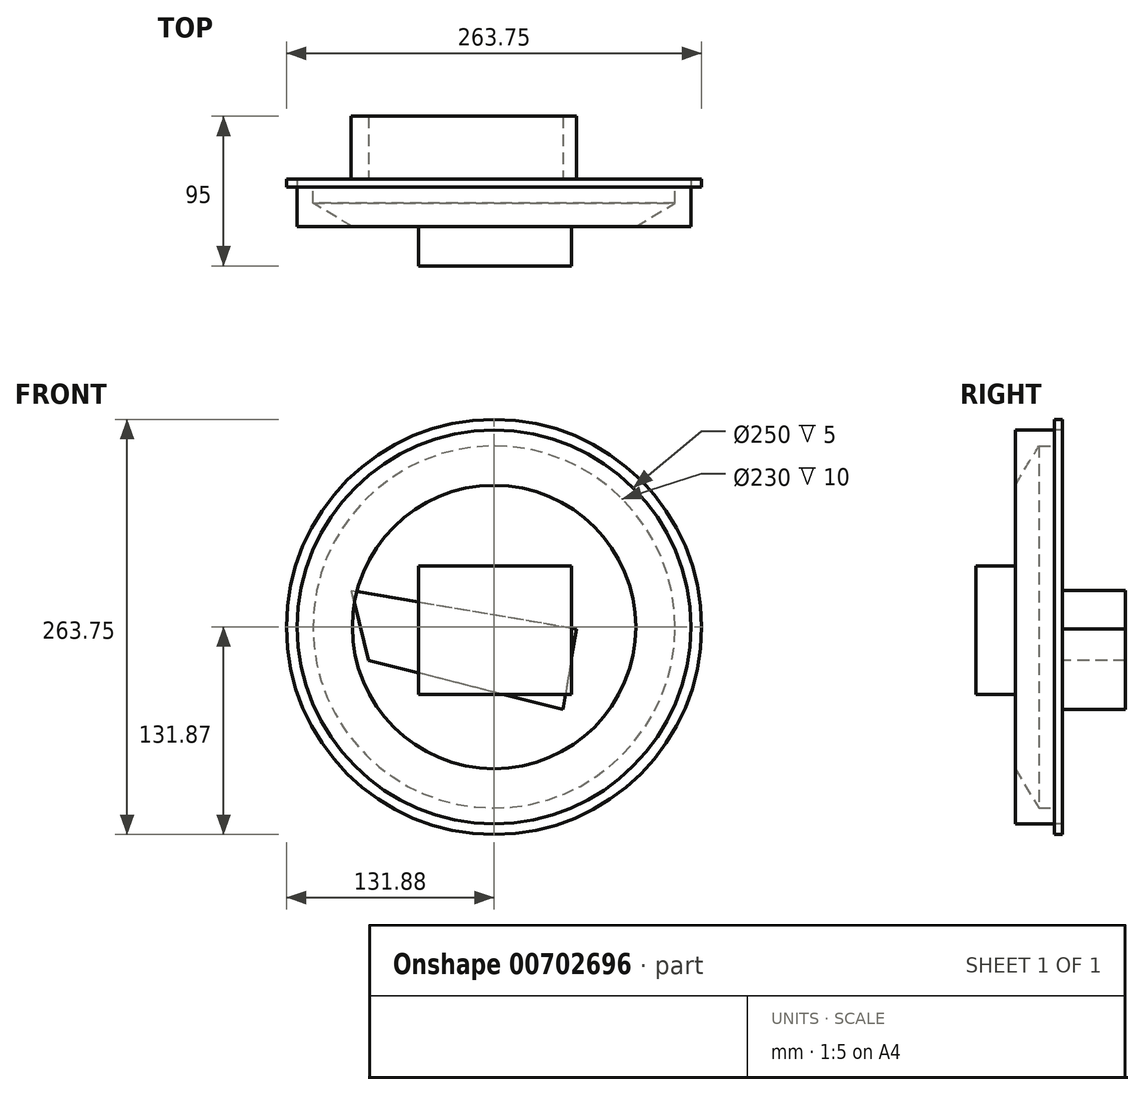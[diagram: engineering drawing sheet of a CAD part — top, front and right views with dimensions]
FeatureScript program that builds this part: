
annotation { "Feature Type Name" : "Feature", "Feature Type Description" : "" }
export const myFeature = defineFeature(function(context is Context, id is Id, definition is map)
    precondition{}
    {
        {
            var Q0;
            Q0=qCreatedBy(makeId("Front.planeOp"),FACE);
            var sketch = newSketch(context, id + "F0", { "sketchPlane" : qUnion([Q0])});
            skCircle(sketch, "E0", {"center": v(-49.3, 42.83) * mm, "radius": 125 * mm});
            skSolve(sketch);
        }
        {
            var Q0;
            Q0=makeQuery(id+"F0.imprint","IMPRINT",FACE,{"disambiguationData":[TD([[makeQuery(id+"F0.imprint","IMPRINT",EDGE,{"derivedFrom":sQuery(id+"F0.wireOp",EDGE,"E0")}),1.0]])]});
            extrude(context, id + "F1", {"entities" : qUnion([Q0]), "depth" : 150 * mm, "offsetDistance" : 25 * mm});
        }
        {
            var Q0;
            Q0=makeQuery(id+"F1.opExtrude","CAP_FACE",FACE,{"disambiguationData":[OSD([sQuery(id+"F0.wireOp",EDGE,"E0")])],"isStart":true});
            var sketch = newSketch(context, id + "F2", { "sketchPlane" : qUnion([Q0])});
            skPoint(sketch, "E1", {"position": v(49.3, 42.83) * mm});
            skCircle(sketch, "E2", {"center": v(49.3, 42.83) * mm, "radius": 131.88 * mm});
            skSolve(sketch);
        }
        {
            var Q0;
            Q0=makeQuery(id+"F2.imprint","IMPRINT",FACE,{"disambiguationData":[TD([[makeQuery(id+"F2.imprint","IMPRINT",EDGE,{"derivedFrom":sQuery(id+"F2.wireOp",EDGE,"E2")}),1.0]])]});
            extrude(context, id + "F3", {"entities" : qUnion([Q0]), "depth" : 5 * mm, "offsetDistance" : 25 * mm});
        }
        {
            var Q0;
            Q0=makeQuery(id+"F1.opExtrude","CAP_FACE",FACE,{"disambiguationData":[OSD([sQuery(id+"F0.wireOp",EDGE,"E0")])],"isStart":true});
            var sketch = newSketch(context, id + "F4", { "sketchPlane" : qUnion([Q0])});
            skPoint(sketch, "E3", {"position": v(49.3, 42.83) * mm});
            skSolve(sketch);
        }
        {
            var Q0;
            Q0=sQuery(id+"F4.wireOp",VERTEX,"E3");
            var Q1;
            Q1=makeQuery(id+"F1.opExtrude","SWEPT_BODY",BODY,{"disambiguationData":[OSD([sQuery(id+"F0.wireOp",EDGE,"E0")])]});
            hole(context, id + "F5", {"style" : HoleStyle.SIMPLE, "endStyle" : HoleEndStyle.BLIND, "holeDiameter" : 230 * mm, "majorDiameter" : 5 * mm, "holeDepth" : 10 * mm, "isTappedThrough" : true, "tappedDepth" : 12 * mm, "tapClearance" : 3, "locations" : qUnion([Q0]), "scope" : qUnion([Q1])});
        }
        {
            var Q0;
            Q0=makeQuery(id+"F1.opExtrude","CAP_FACE",FACE,{"disambiguationData":[OSD([sQuery(id+"F0.wireOp",EDGE,"E0")])],"isStart":false});
            extrude(context, id + "F6", {"entities" : qUnion([Q0]), "operationType" : NewBodyOperationType.ADD, "depth" : 25 * mm, "offsetDistance" : 25 * mm});
        }
        {
            var Q0;
            Q0=makeQuery(id+"F6.opExtrude","CAP_FACE",FACE,{"disambiguationData":[OSD([sQuery(id+"F0.wireOp",EDGE,"E0")])],"isStart":false});
            extrude(context, id + "F7", {"entities" : qUnion([Q0]), "operationType" : NewBodyOperationType.REMOVE, "oppositeDirection" : true, "depth" : 150 * mm, "offsetDistance" : 25 * mm});
        }
        {
            var Q0;
            Q0=makeQuery(id+"F3.opExtrude","CAP_FACE",FACE,{"disambiguationData":[OSD([sQuery(id+"F0.wireOp",EDGE,"E0"),sQuery(id+"F2.wireOp",EDGE,"E2")])],"isStart":false});
            var sketch = newSketch(context, id + "F8", { "sketchPlane" : qUnion([Q0])});
            skLineSegment(sketch, "E4", {"start": v(140.06, 66.11) * mm, "end": v(-3.13, 41.73) * mm});
            skLineSegment(sketch, "E5", {"start": v(-3.13, 41.73) * mm, "end": v(5.62, -9.68) * mm});
            skLineSegment(sketch, "E6", {"start": v(5.62, -9.68) * mm, "end": v(129.1, 21.7) * mm});
            skLineSegment(sketch, "E7", {"start": v(129.1, 21.7) * mm, "end": v(140.06, 66.11) * mm});
            skSolve(sketch);
        }
        {
            var Q0;
            Q0=makeQuery(id+"F8.imprint","IMPRINT",FACE,{"disambiguationData":[TD([[makeQuery(id+"F8.imprint","IMPRINT",EDGE,{"derivedFrom":sQuery(id+"F8.wireOp",EDGE,"E4")}),1.0]])]});
            extrude(context, id + "F9", {"entities" : qUnion([Q0]), "depth" : 40 * mm, "offsetDistance" : 25 * mm});
        }
        {
            var Q0;
            Q0=makeQuery(id+"F7.boolean.opBoolean","COPY",FACE,{"derivedFrom":makeQuery(id+"F7.opExtrude","CAP_FACE",FACE,{"disambiguationData":[OSD([sQuery(id+"F0.wireOp",EDGE,"E0")])],"isStart":false})});
            var sketch = newSketch(context, id + "F10", { "sketchPlane" : qUnion([Q0])});
            skLineSegment(sketch, "E8.bottom", {"start": v(-97.12, 81.46) * mm, "end": v(0, 81.46) * mm});
            skLineSegment(sketch, "E8.top", {"start": v(-97.12, 0) * mm, "end": v(0, 0) * mm});
            skLineSegment(sketch, "E8.left", {"start": v(-97.12, 81.46) * mm, "end": v(-97.12, 0) * mm});
            skLineSegment(sketch, "E8.right", {"start": v(0, 81.46) * mm, "end": v(0, 0) * mm});
            skSolve(sketch);
        }
        {
            var Q0;
            Q0 = qSketchRegion(id + "F10", true);
            extrude(context, id + "F11", {"entities" : qUnion([Q0]), "depth" : 25 * mm, "offsetDistance" : 25 * mm});
        }
    });
